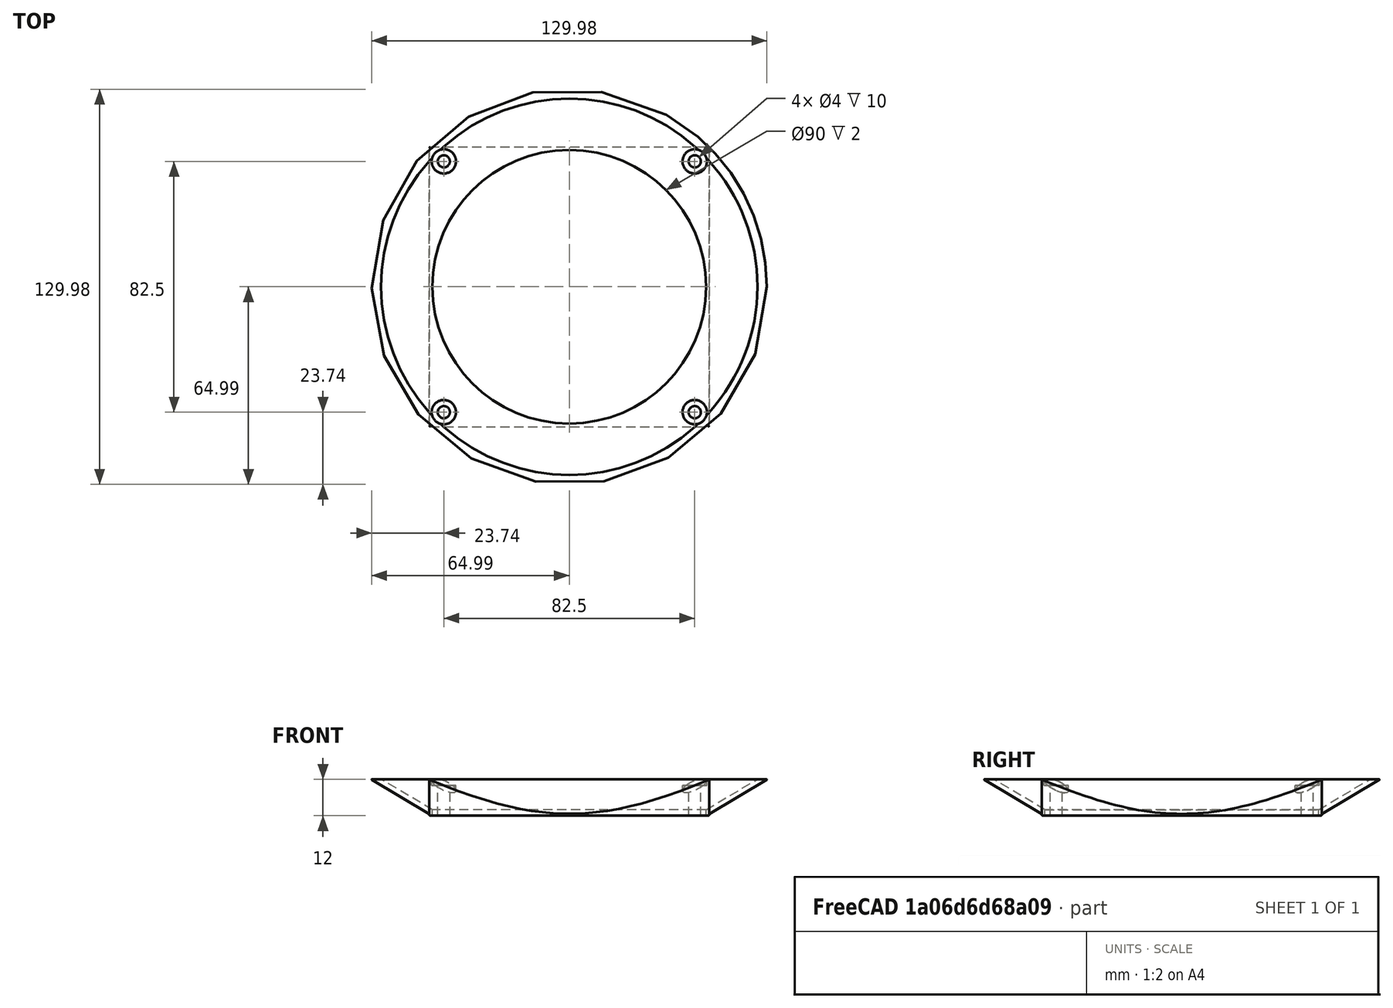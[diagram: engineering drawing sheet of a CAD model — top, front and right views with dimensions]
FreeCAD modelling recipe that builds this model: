
FCSTD DOCUMENT  (FreeCAD 0.18R16117 (Git))
Label: fan duct
License: All rights reserved
LicenseURL: http://en.wikipedia.org/wiki/All_rights_reserved
objects: Part::Cylinder×13, Part::MultiFuse×5, Part::Cut×3, Part::Cone×2, Part::Fillet×2, Part::Box×1, App::MeasureDistance×1
note: 26 computed .brp shape members not serialized (recipe doc carries the construction recipe); baked Part::Feature solids carry a one-line shape summary decoded from their .brp

FEATURE [Part::Cone] Cone
  Angle = 360
  AttacherType = Attacher::AttachEngine3D
  Height = 12
  Radius1 = 45
  Radius2 = 65.25
FEATURE [Part::Cone] Cone001
  Angle = 360
  AttacherType = Attacher::AttachEngine3D
  Height = 12
  Placement = pos=(0,0,2) rot=(0,0,1;0rad)
  Radius1 = 45
  Radius2 = 65.25
FEATURE [Part::Box] Box  label="Cube"
  AttacherType = Attacher::AttachEngine3D
  Height = 12
  Length = 92
  Placement = pos=(-46,-46,0) rot=(0,0,1;0rad)
  Width = 92
FEATURE [Part::Cylinder] Cylinder
  Angle = 360
  AttacherType = Attacher::AttachEngine3D
  Height = 15
  Placement = pos=(0,0,-1) rot=(0,0,1;0rad)
  Radius = 45
FEATURE [Part::Fillet] Fillet
  Base = -> Box
  Edges = 8 edges r=0.3: [Edge1,Edge3,Edge4,Edge5,Edge7,Edge8,Edge9,Edge11]
FEATURE [Part::Fillet] Fillet001
  Base = -> Cone
  Edges = 1 edges r=0.1: [Edge1]
FEATURE [Part::MultiFuse] Fusion
  Shapes = -> [Fillet,Fillet001]
FEATURE [Part::MultiFuse] Fusion001  label="void"
  Shapes = -> [Cylinder,Cone001]
FEATURE [Part::Cut] Cut
  Base = -> Fusion
  Tool = -> Fusion001
FEATURE [Part::Cylinder] Cylinder001
  Angle = 360
  AttacherType = Attacher::AttachEngine3D
  Height = 10
  Placement = pos=(41.25,41.25,0) rot=(0,0,1;0rad)
  Radius = 4
FEATURE [Part::Cylinder] Cylinder002
  Angle = 360
  AttacherType = Attacher::AttachEngine3D
  Height = 10
  Placement = pos=(-41.25,41.25,0) rot=(0,0,1;0rad)
  Radius = 4
FEATURE [Part::Cylinder] Cylinder003
  Angle = 360
  AttacherType = Attacher::AttachEngine3D
  Height = 10
  Placement = pos=(41.25,-41.25,0) rot=(0,0,1;0rad)
  Radius = 4
FEATURE [Part::Cylinder] Cylinder004
  Angle = 360
  AttacherType = Attacher::AttachEngine3D
  Height = 10
  Placement = pos=(-41.25,-41.25,0) rot=(0,0,1;0rad)
  Radius = 4
FEATURE [Part::Cylinder] Cylinder005
  Angle = 360
  AttacherType = Attacher::AttachEngine3D
  Height = 17
  Placement = pos=(41.25,41.25,-3) rot=(0,0,1;0rad)
  Radius = 2
FEATURE [Part::Cylinder] Cylinder006
  Angle = 360
  AttacherType = Attacher::AttachEngine3D
  Height = 17
  Placement = pos=(-41.25,41.25,-3) rot=(0,0,1;0rad)
  Radius = 2
FEATURE [Part::Cylinder] Cylinder007
  Angle = 360
  AttacherType = Attacher::AttachEngine3D
  Height = 17
  Placement = pos=(41.25,-41.25,-3) rot=(0,0,1;0rad)
  Radius = 2
FEATURE [Part::Cylinder] Cylinder008
  Angle = 360
  AttacherType = Attacher::AttachEngine3D
  Height = 17
  Placement = pos=(-41.25,-41.25,-3) rot=(0,0,1;0rad)
  Radius = 2
FEATURE [Part::MultiFuse] Fusion002
  Shapes = -> [Cut,Cylinder004,Cylinder003,Cylinder002,Cylinder001]
FEATURE [Part::MultiFuse] Fusion003
  Shapes = -> [Cylinder008,Cylinder007,Cylinder005,Cylinder006]
FEATURE [Part::Cut] Cut001
  Base = -> Fusion002
  Tool = -> Fusion003
FEATURE [Part::Cylinder] Cylinder009
  Angle = 360
  AttacherType = Attacher::AttachEngine3D
  Height = 4
  Placement = pos=(41.25,41.25,10) rot=(0,0,1;0rad)
  Radius = 4
FEATURE [Part::Cylinder] Cylinder010
  Angle = 360
  AttacherType = Attacher::AttachEngine3D
  Height = 4
  Placement = pos=(-41.25,41.25,10) rot=(0,0,1;0rad)
  Radius = 4
FEATURE [Part::Cylinder] Cylinder011
  Angle = 360
  AttacherType = Attacher::AttachEngine3D
  Height = 4
  Placement = pos=(-41.25,-41.25,10) rot=(0,0,1;0rad)
  Radius = 4
FEATURE [Part::Cylinder] Cylinder012
  Angle = 360
  AttacherType = Attacher::AttachEngine3D
  Height = 4
  Placement = pos=(41.25,-41.25,10) rot=(0,0,1;0rad)
  Radius = 4
FEATURE [Part::MultiFuse] Fusion004
  Shapes = -> [Cylinder012,Cylinder009,Cylinder011,Cylinder010]
FEATURE [Part::Cut] Cut002
  Base = -> Cut001
  Tool = -> Fusion004
FEATURE [App::MeasureDistance] Distance  label="Distance: 10.00 mm"
  Distance = 10.0008
  P1 = (42.9564,-42.2701,10)
  P2 = (42.884,-42.3778,0)
